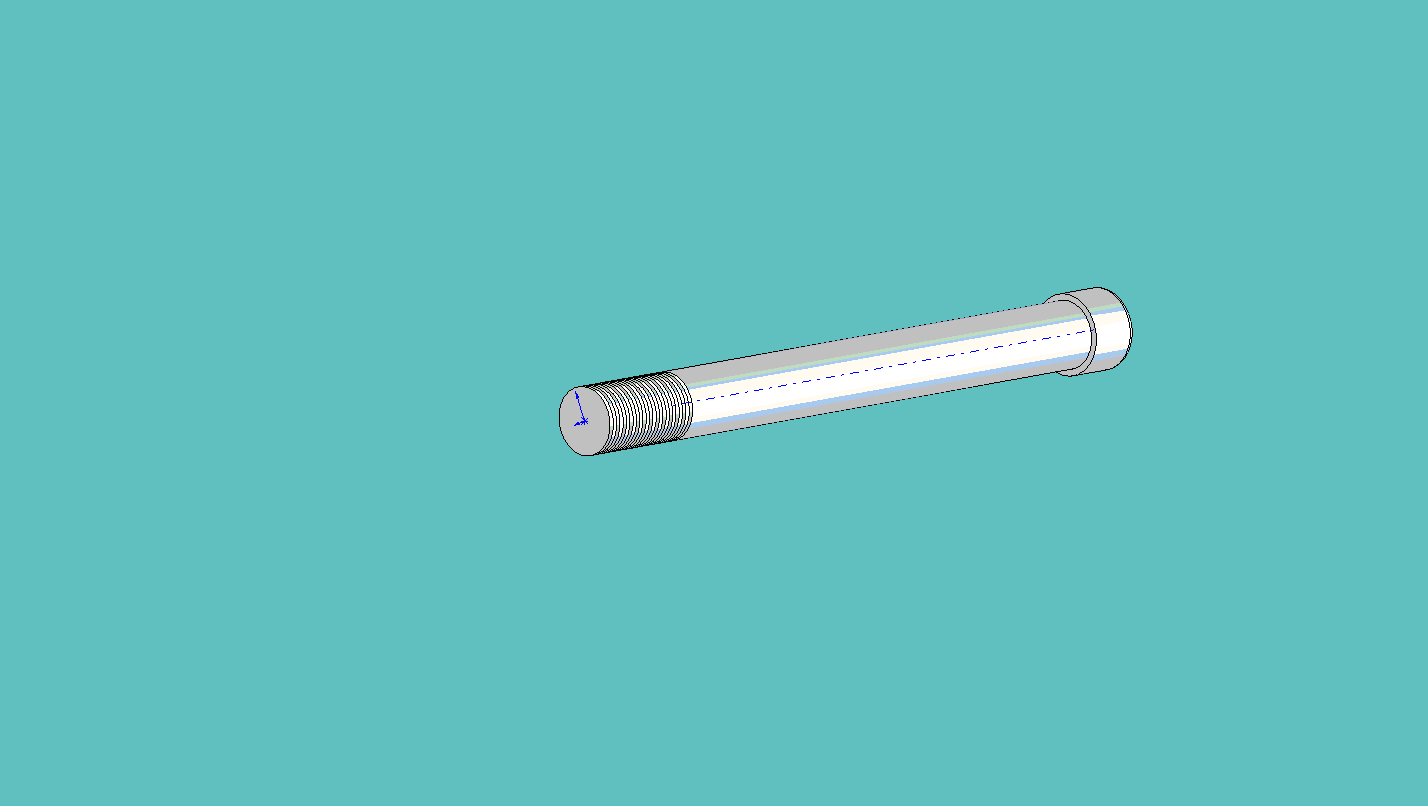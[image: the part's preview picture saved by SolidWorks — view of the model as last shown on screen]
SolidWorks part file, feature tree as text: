
SOLIDWORKS PART (.sldprt)
format: sldprt  version: not decoded by parser v0  size: 150,016 bytes
history: native  units: mm
features: sketch x4, extrude x2, material x1, fillet x1, cut_extrude x1, cut_revolve x1, pattern_linear x1 (+13 scaffold rows collapsed)
feature tree (24):
  scaffold x13  (default folders/planes/origin — collapsed)
  material  "Material <not specified>"
  sketch  "Sketch1"  dims[D1=12.6mm]
  extrude  "Extrude1"  Depth=127mm
  sketch  "Sketch2"  dims[D1=~14.972427mm]
  extrude  "Extrude2"  Depth=10.18mm
  fillet  "Fillet1"  Radius=1.27mm
  sketch  "Sketch3"
  cut_extrude  "Cut-Extrude1"  Depth=10.18mm
  sketch  "Sketch4"
  cut_revolve  "Cut-Revolve1"  Angle=360deg
  pattern_linear  "LPattern1"  Count1=13 Count2=1 Spacing1=1.74mm Spacing2=50mm
decode coverage: 8 of 10 modeling features carry decoded parameters
note: ~ marks probable driven/reference dimensions
note: suppression state not decoded; provenance and decode notes live in map.json
